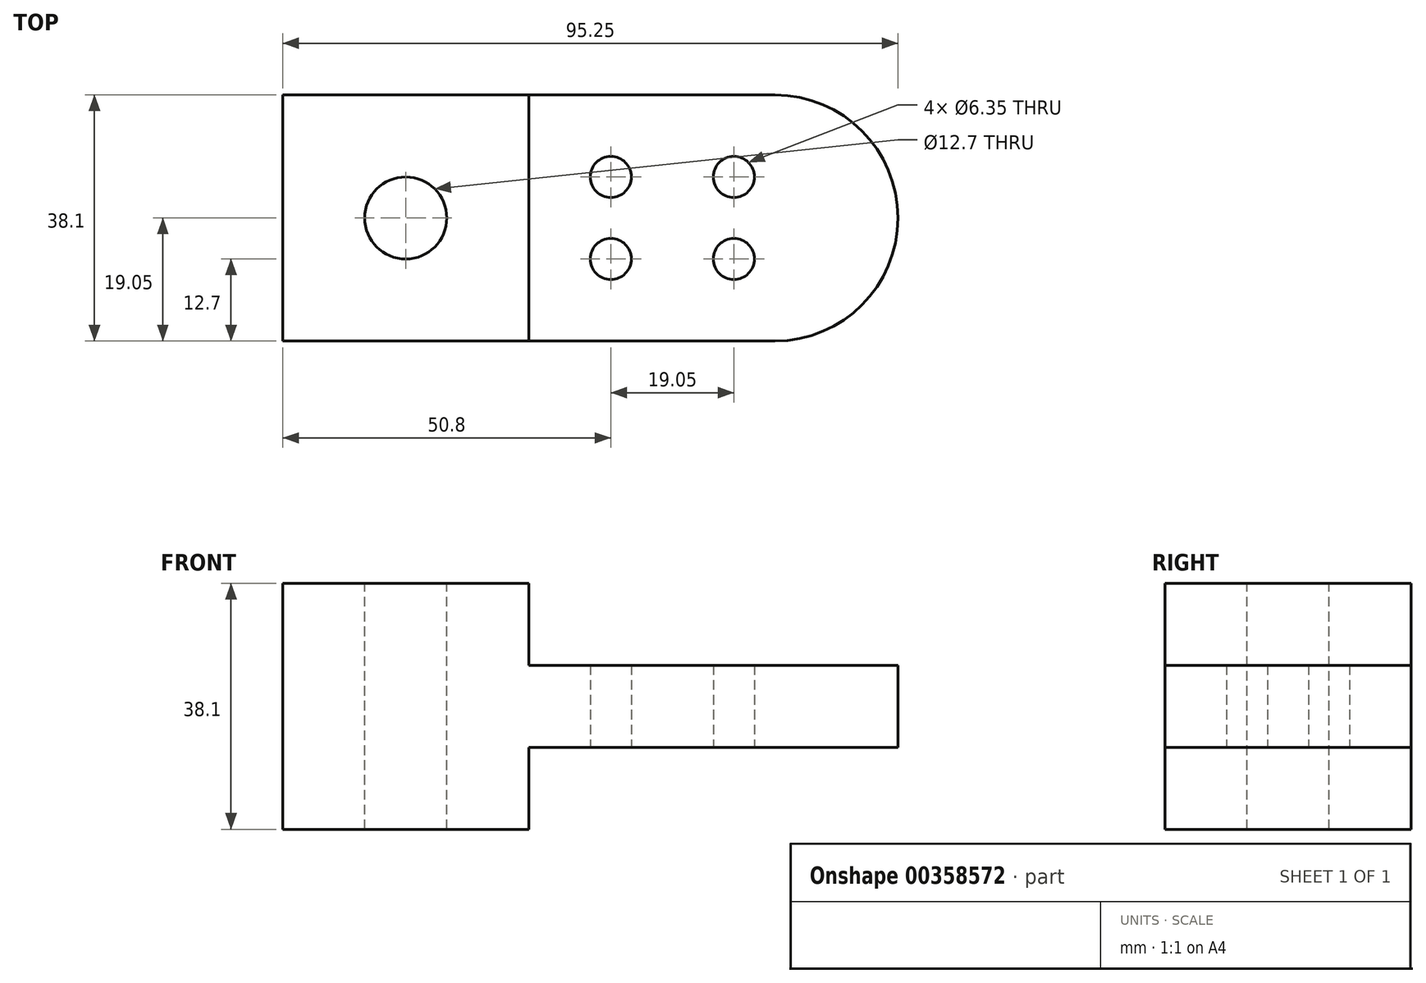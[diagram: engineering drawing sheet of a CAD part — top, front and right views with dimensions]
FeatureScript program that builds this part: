
annotation { "Feature Type Name" : "Feature", "Feature Type Description" : "" }
export const myFeature = defineFeature(function(context is Context, id is Id, definition is map)
    precondition{}
    {
        {
            var Q0;
            Q0=qCreatedBy(makeId("Top.planeOp"),FACE);
            var sketch = newSketch(context, id + "F0", { "sketchPlane" : qUnion([Q0])});
            skLineSegment(sketch, "E0.bottom", {"start": v(0, 0) * mm, "end": v(38.1, 0) * mm});
            skLineSegment(sketch, "E0.top", {"start": v(0, 38.1) * mm, "end": v(38.1, 38.1) * mm});
            skLineSegment(sketch, "E0.left", {"start": v(0, 0) * mm, "end": v(0, 38.1) * mm});
            skLineSegment(sketch, "E0.right", {"start": v(38.1, 0) * mm, "end": v(38.1, 38.1) * mm});
            skSolve(sketch);
        }
        {
            var Q0;
            Q0 = qSketchRegion(id + "F0", true);
            extrude(context, id + "F1", {"entities" : qUnion([Q0]), "depth" : 12.7 * mm});
        }
        {
            var Q0;
            Q0=makeQuery(id+"F1.opExtrude","CAP_FACE",FACE,{"disambiguationData":[OSD([sQuery(id+"F0.wireOp",EDGE,"E0.bottom"),sQuery(id+"F0.wireOp",EDGE,"E0.top"),sQuery(id+"F0.wireOp",EDGE,"E0.left"),sQuery(id+"F0.wireOp",EDGE,"E0.right")])],"isStart":false});
            var sketch = newSketch(context, id + "F2", { "sketchPlane" : qUnion([Q0])});
            skLineSegment(sketch, "E1", {"start": v(0, 0) * mm, "end": v(0, 38.1) * mm});
            skLineSegment(sketch, "E2", {"start": v(0, 38.1) * mm, "end": v(76.2, 38.1) * mm});
            skArc(sketch, "E3", {"start": v(76.2, 0) * mm, "mid": v(95.25, 19.05) * mm, "end": v(76.2, 38.1) * mm});
            skLineSegment(sketch, "E4", {"start": v(0, 0) * mm, "end": v(76.2, 0) * mm});
            skCircle(sketch, "E5", {"center": v(50.8, 25.4) * mm, "radius": 3.18 * mm});
            skCircle(sketch, "E6", {"center": v(69.85, 25.4) * mm, "radius": 3.18 * mm});
            skCircle(sketch, "E7", {"center": v(69.85, 12.7) * mm, "radius": 3.18 * mm});
            skCircle(sketch, "E8", {"center": v(50.8, 12.7) * mm, "radius": 3.18 * mm});
            skSolve(sketch);
        }
        {
            var Q0;
            Q0 = qSketchRegion(id + "F2", true);
            extrude(context, id + "F3", {"entities" : qUnion([Q0]), "operationType" : NewBodyOperationType.ADD, "depth" : 12.7 * mm});
        }
        {
            var Q0;
            Q0 = qSketchRegion(id + "F2", true);
            extrude(context, id + "F4", {"entities" : qUnion([Q0]), "operationType" : NewBodyOperationType.ADD, "depth" : 12.7 * mm});
        }
        {
            var Q0;
            Q0=makeQuery(id+"F3.opExtrude","CAP_FACE",FACE,{"disambiguationData":[OSD([sQuery(id+"F2.wireOp",EDGE,"E1"),sQuery(id+"F2.wireOp",EDGE,"E2"),sQuery(id+"F2.wireOp",EDGE,"E3"),sQuery(id+"F2.wireOp",EDGE,"E4"),sQuery(id+"F2.wireOp",EDGE,"E5"),sQuery(id+"F2.wireOp",EDGE,"E6"),sQuery(id+"F2.wireOp",EDGE,"E7"),sQuery(id+"F2.wireOp",EDGE,"E8")])],"isStart":false});
            var sketch = newSketch(context, id + "F5", { "sketchPlane" : qUnion([Q0])});
            skLineSegment(sketch, "E9.bottom", {"start": v(0, 0) * mm, "end": v(38.1, 0) * mm});
            skLineSegment(sketch, "E9.top", {"start": v(0, 38.1) * mm, "end": v(38.1, 38.1) * mm});
            skLineSegment(sketch, "E9.left", {"start": v(0, 0) * mm, "end": v(0, 38.1) * mm});
            skLineSegment(sketch, "E9.right", {"start": v(38.1, 0) * mm, "end": v(38.1, 38.1) * mm});
            skSolve(sketch);
        }
        {
            var Q0;
            Q0 = qSketchRegion(id + "F5", true);
            extrude(context, id + "F6", {"entities" : qUnion([Q0]), "operationType" : NewBodyOperationType.ADD, "depth" : 12.7 * mm});
        }
        {
            var Q0;
            Q0=makeQuery(id+"F6.opExtrude","CAP_FACE",FACE,{"disambiguationData":[OSD([sQuery(id+"F5.wireOp",EDGE,"E9.bottom"),sQuery(id+"F5.wireOp",EDGE,"E9.top"),sQuery(id+"F5.wireOp",EDGE,"E9.left"),sQuery(id+"F5.wireOp",EDGE,"E9.right")])],"isStart":false});
            var sketch = newSketch(context, id + "F7", { "sketchPlane" : qUnion([Q0])});
            skCircle(sketch, "E10", {"center": v(19.05, 19.05) * mm, "radius": 6.35 * mm});
            skSolve(sketch);
        }
        {
            var Q0;
            Q0 = qSketchRegion(id + "F7", true);
            extrude(context, id + "F8", {"entities" : qUnion([Q0]), "operationType" : NewBodyOperationType.REMOVE, "oppositeDirection" : true, "depth" : 50.8 * mm});
        }
    });
